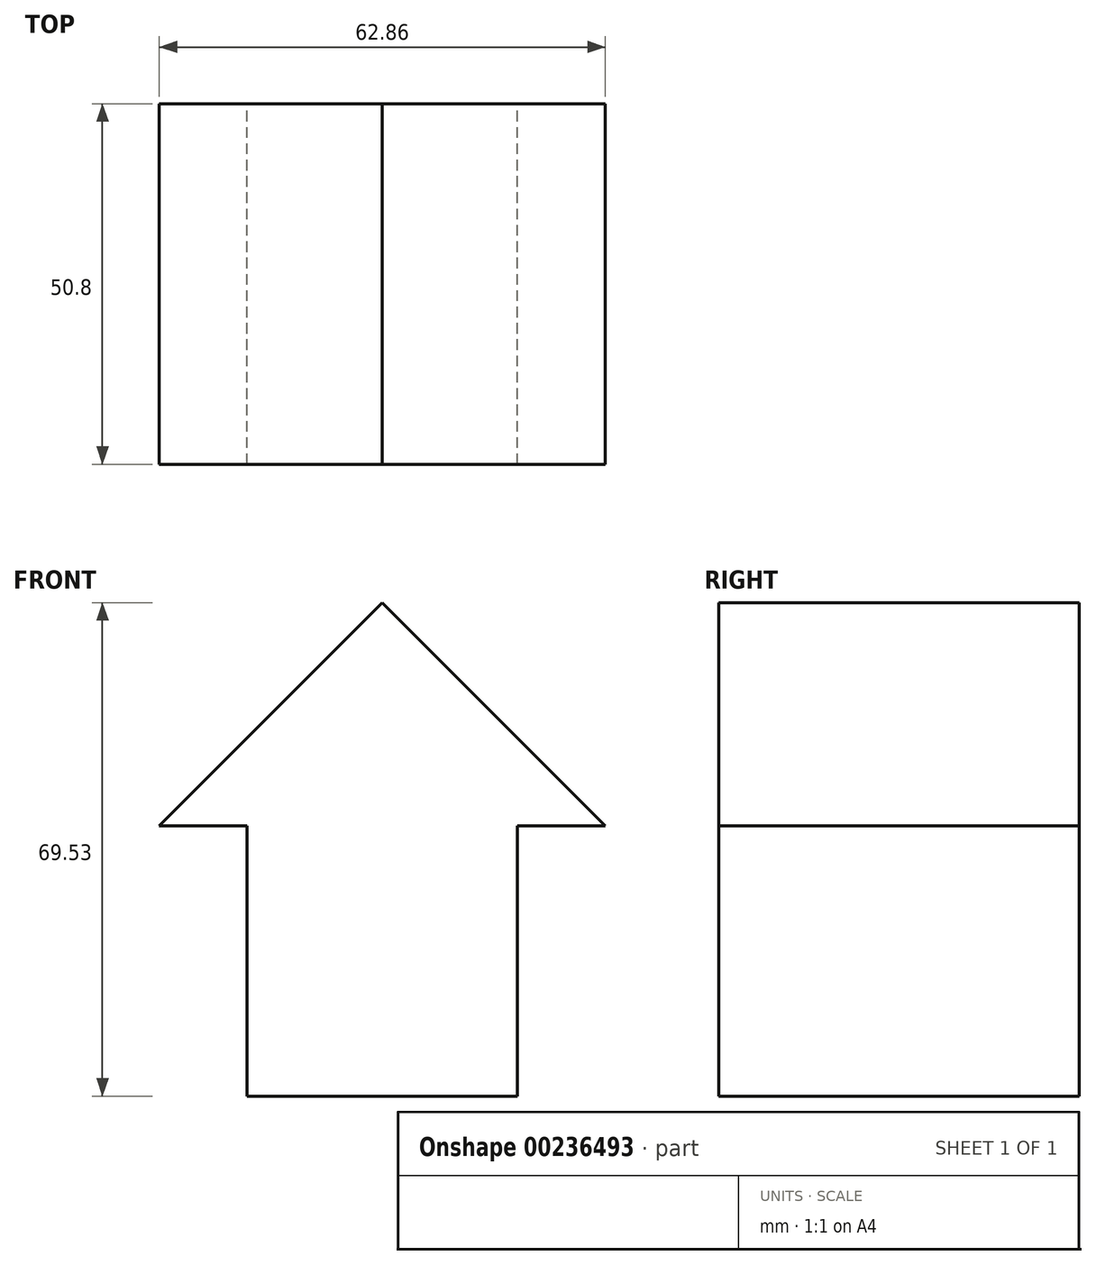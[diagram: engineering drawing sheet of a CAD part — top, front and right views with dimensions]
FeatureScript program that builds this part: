
annotation { "Feature Type Name" : "Feature", "Feature Type Description" : "" }
export const myFeature = defineFeature(function(context is Context, id is Id, definition is map)
    precondition{}
    {
        {
            var Q0;
            Q0=qCreatedBy(makeId("Front.planeOp"),FACE);
            var sketch = newSketch(context, id + "F0", { "sketchPlane" : qUnion([Q0])});
            skLineSegment(sketch, "E0.bottom", {"start": v(0, 0) * mm, "end": v(38.1, 0) * mm});
            skLineSegment(sketch, "E0.top", {"start": v(0, 38.1) * mm, "end": v(38.1, 38.1) * mm});
            skLineSegment(sketch, "E0.left", {"start": v(0, 0) * mm, "end": v(0, 38.1) * mm});
            skLineSegment(sketch, "E0.right", {"start": v(38.1, 0) * mm, "end": v(38.1, 38.1) * mm});
            skCircle(sketch, "E1", {"center": v(19.05, 19.05) * mm, "radius": 6.59 * mm});
            skPoint(sketch, "E1.centerSnap0", {"position": v(0, 19.05) * mm});
            skPoint(sketch, "E1.centerSnap1", {"position": v(19.05, 38.1) * mm});
            skLineSegment(sketch, "E2", {"start": v(38.1, 38.1) * mm, "end": v(50.48, 38.1) * mm});
            skLineSegment(sketch, "E3", {"start": v(50.48, 38.1) * mm, "end": v(19.05, 69.53) * mm});
            skLineSegment(sketch, "E4", {"start": v(19.05, 69.53) * mm, "end": v(-12.38, 38.1) * mm});
            skLineSegment(sketch, "E5", {"start": v(-12.38, 38.1) * mm, "end": v(0, 38.1) * mm});
            skSolve(sketch);
        }
        {
            var Q0;
            Q0 = qSketchRegion(id + "F0", true);
            var Q1;
            Q1=makeQuery(id+"F0.imprint","IMPRINT",FACE,{"disambiguationData":[TD([[makeQuery(id+"F0.imprint","IMPRINT",EDGE,{"derivedFrom":sQuery(id+"F0.wireOp",EDGE,"E1")}),1.0]])]});
            extrude(context, id + "F1", {"entities" : qUnion([Q0, Q1]), "depth" : 50.8 * mm});
        }
    });
